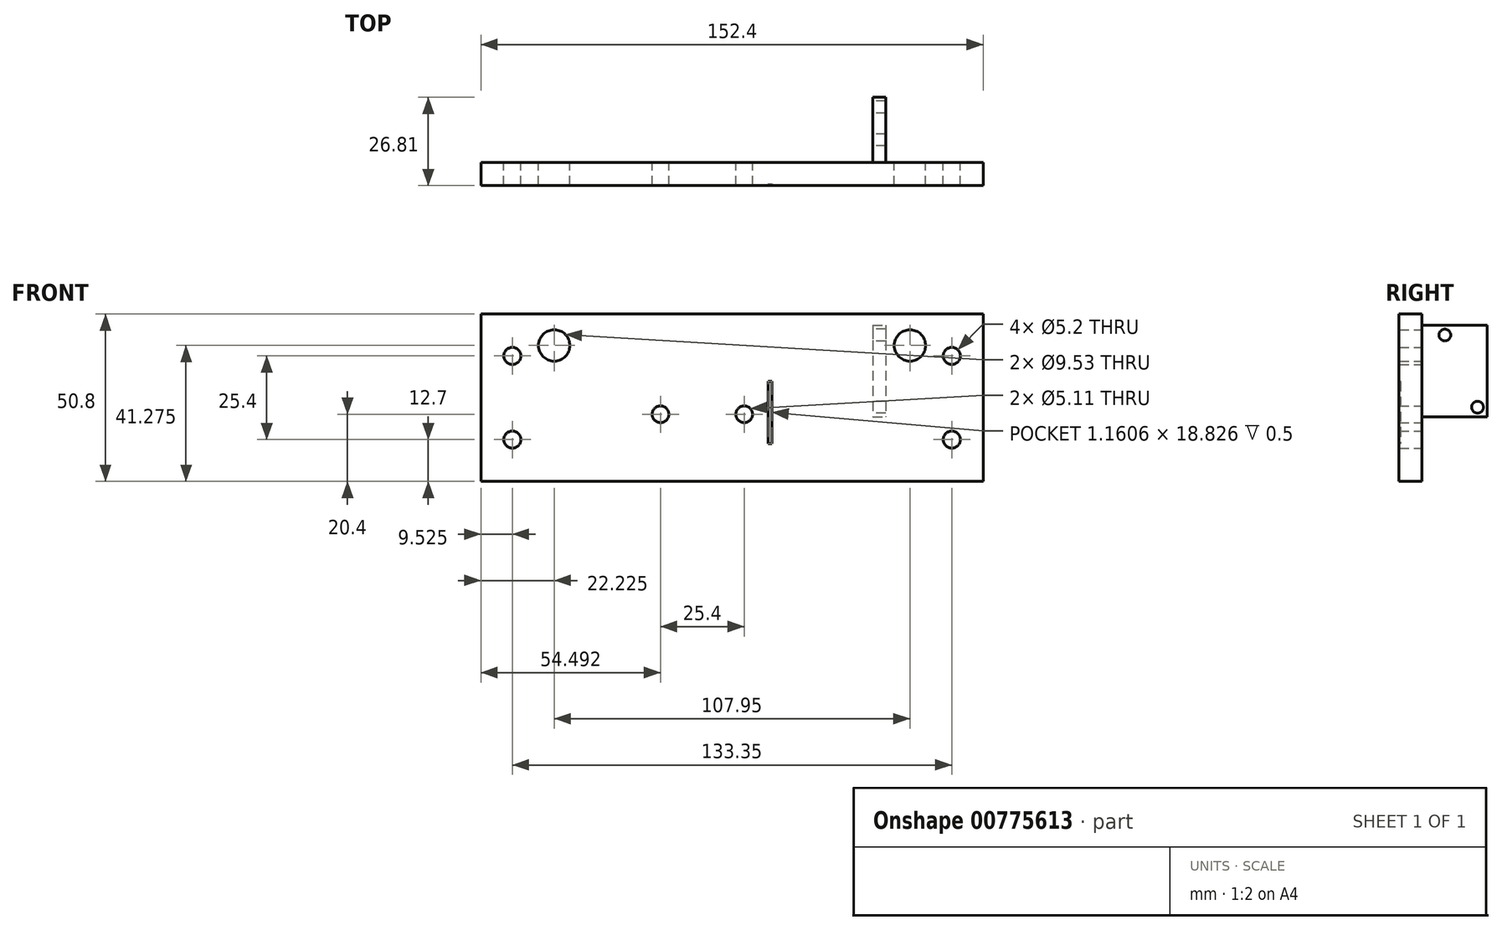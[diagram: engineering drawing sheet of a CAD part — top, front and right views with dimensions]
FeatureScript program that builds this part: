
annotation { "Feature Type Name" : "Feature", "Feature Type Description" : "" }
export const myFeature = defineFeature(function(context is Context, id is Id, definition is map)
    precondition{}
    {
        {
            var Q0;
            Q0=qCreatedBy(makeId("Front.planeOp"),FACE);
            var sketch = newSketch(context, id + "F0", { "sketchPlane" : qUnion([Q0])});
            skLineSegment(sketch, "E0.bottom", {"start": v(76.2, -25.4) * mm, "end": v(-76.2, -25.4) * mm});
            skLineSegment(sketch, "E0.top", {"start": v(76.2, 25.4) * mm, "end": v(-76.2, 25.4) * mm});
            skLineSegment(sketch, "E0.left", {"start": v(76.2, -25.4) * mm, "end": v(76.2, 25.4) * mm});
            skLineSegment(sketch, "E0.right", {"start": v(-76.2, -25.4) * mm, "end": v(-76.2, 25.4) * mm});
            skCircle(sketch, "E1", {"center": v(-66.68, -12.7) * mm, "radius": 2.6 * mm});
            skCircle(sketch, "E2", {"center": v(-66.68, 12.7) * mm, "radius": 2.6 * mm});
            skCircle(sketch, "E3", {"center": v(66.67, 12.7) * mm, "radius": 2.6 * mm});
            skCircle(sketch, "E4", {"center": v(66.67, -12.7) * mm, "radius": 2.6 * mm});
            skCircle(sketch, "E5", {"center": v(-53.98, 15.88) * mm, "radius": 4.76 * mm});
            skCircle(sketch, "E6", {"center": v(53.97, 15.88) * mm, "radius": 4.76 * mm});
            skLineSegment(sketch, "E7", {"start": v(-76.2, 0) * mm, "end": v(76.2, 0) * mm});
            skCircle(sketch, "E8", {"center": v(3.7, -5) * mm, "radius": 2.55 * mm});
            skCircle(sketch, "E9", {"center": v(-21.7, -5) * mm, "radius": 2.55 * mm});
            skSolve(sketch);
        }
        {
            var Q0;
            Q0=qSketchRegion(id+"F0",true);
            extrude(context, id + "F1", {"entities" : qUnion([Q0]), "depth" : 7 * mm, "offsetDistance" : 25.4 * mm});
        }
        {
            var Q0;
            Q0=makeQuery(id+"F1.opExtrude","CAP_FACE",FACE,{"disambiguationData":[OSD([sQuery(id+"F0.wireOp",EDGE,"E0.bottom"),sQuery(id+"F0.wireOp",EDGE,"E0.top"),sQuery(id+"F0.wireOp",EDGE,"E0.left"),sQuery(id+"F0.wireOp",EDGE,"E0.right"),sQuery(id+"F0.wireOp",EDGE,"E1"),sQuery(id+"F0.wireOp",EDGE,"E2"),sQuery(id+"F0.wireOp",EDGE,"E3"),sQuery(id+"F0.wireOp",EDGE,"E4"),sQuery(id+"F0.wireOp",EDGE,"E5"),sQuery(id+"F0.wireOp",EDGE,"E6"),sQuery(id+"F0.wireOp",EDGE,"E8"),sQuery(id+"F0.wireOp",EDGE,"E9")])],"isStart":false});
            var sketch = newSketch(context, id + "F2", { "sketchPlane" : qUnion([Q0])});
            skSolve(sketch);
        }
        {
            var Q0;
            Q0 = qSketchRegion(id + "F0", true);
            extrude(context, id + "F3", {"entities" : qUnion([Q0]), "operationType" : NewBodyOperationType.REMOVE, "oppositeDirection" : true, "depth" : 0.2 * mm, "offsetDistance" : 25.4 * mm});
        }
        {
            var Q0;
            Q0=makeQuery(id+"F2.imprint","IMPRINT",FACE,{"disambiguationData":[TD([[makeQuery(id+"F2.imprint","IMPRINT",EDGE,{"derivedFrom":makeQuery(id+"F1.opExtrude","CAP_EDGE",EDGE,{"disambiguationData":[OSD([sQuery(id+"F0.wireOp",EDGE,"E0.bottom")])],"isStart":false})}),-1.0]])]});
            var sketch = newSketch(context, id + "F4", { "sketchPlane" : qUnion([Q0])});
            skLineSegment(sketch, "E10.bottom", {"start": v(10.97, 4.96) * mm, "end": v(12.13, 4.96) * mm});
            skLineSegment(sketch, "E10.top", {"start": v(10.97, -13.86) * mm, "end": v(12.13, -13.86) * mm});
            skLineSegment(sketch, "E10.left", {"start": v(10.97, 4.96) * mm, "end": v(10.97, -13.86) * mm});
            skLineSegment(sketch, "E10.right", {"start": v(12.13, 4.96) * mm, "end": v(12.13, -13.86) * mm});
            skSolve(sketch);
        }
        {
            var Q0;
            Q0 = qSketchRegion(id + "F4", true);
            extrude(context, id + "F5", {"entities" : qUnion([Q0]), "operationType" : NewBodyOperationType.REMOVE, "oppositeDirection" : true, "depth" : 0.5 * mm, "offsetDistance" : 25.4 * mm});
        }
        {
            var Q0;
            Q0=makeQuery(id+"F1.opExtrude","CAP_FACE",FACE,{"disambiguationData":[OSD([sQuery(id+"F0.wireOp",EDGE,"E0.bottom"),sQuery(id+"F0.wireOp",EDGE,"E0.top"),sQuery(id+"F0.wireOp",EDGE,"E0.left"),sQuery(id+"F0.wireOp",EDGE,"E0.right"),sQuery(id+"F0.wireOp",EDGE,"E1"),sQuery(id+"F0.wireOp",EDGE,"E2"),sQuery(id+"F0.wireOp",EDGE,"E3"),sQuery(id+"F0.wireOp",EDGE,"E4"),sQuery(id+"F0.wireOp",EDGE,"E5"),sQuery(id+"F0.wireOp",EDGE,"E6"),sQuery(id+"F0.wireOp",EDGE,"E8"),sQuery(id+"F0.wireOp",EDGE,"E9")])],"isStart":true});
            var sketch = newSketch(context, id + "F6", { "sketchPlane" : qUnion([Q0])});
            skLineSegment(sketch, "E11.bottom", {"start": v(-42.68, 22) * mm, "end": v(-46.68, 22) * mm});
            skLineSegment(sketch, "E11.top", {"start": v(-42.68, -5.81) * mm, "end": v(-46.68, -5.81) * mm});
            skLineSegment(sketch, "E11.left", {"start": v(-42.68, 22) * mm, "end": v(-42.68, -5.81) * mm});
            skLineSegment(sketch, "E11.right", {"start": v(-46.68, 22) * mm, "end": v(-46.68, -5.81) * mm});
            skSolve(sketch);
        }
        {
            var Q0;
            Q0 = qSketchRegion(id + "F6", true);
            extrude(context, id + "F7", {"entities" : qUnion([Q0]), "operationType" : NewBodyOperationType.ADD, "depth" : 19.8 * mm, "offsetDistance" : 25.4 * mm});
        }
        {
            var Q0;
            Q0=makeQuery(id+"F7.opExtrude","SWEPT_FACE",FACE,{"disambiguationData":[OSD([sQuery(id+"F6.wireOp",EDGE,"E11.left")])]});
            var sketch = newSketch(context, id + "F8", { "sketchPlane" : qUnion([Q0])});
            skCircle(sketch, "E12", {"center": v(-16.85, -2.86) * mm, "radius": 1.79 * mm});
            skCircle(sketch, "E13", {"center": v(-6.93, 19.04) * mm, "radius": 1.79 * mm});
            skSolve(sketch);
        }
        {
            var Q0;
            Q0 = qSketchRegion(id + "F8", true);
            extrude(context, id + "F9", {"entities" : qUnion([Q0]), "operationType" : NewBodyOperationType.REMOVE, "endBound" : BoundingType.UP_TO_NEXT, "oppositeDirection" : true, "depth" : 25.4 * mm, "offsetDistance" : 25.4 * mm});
        }
    });
